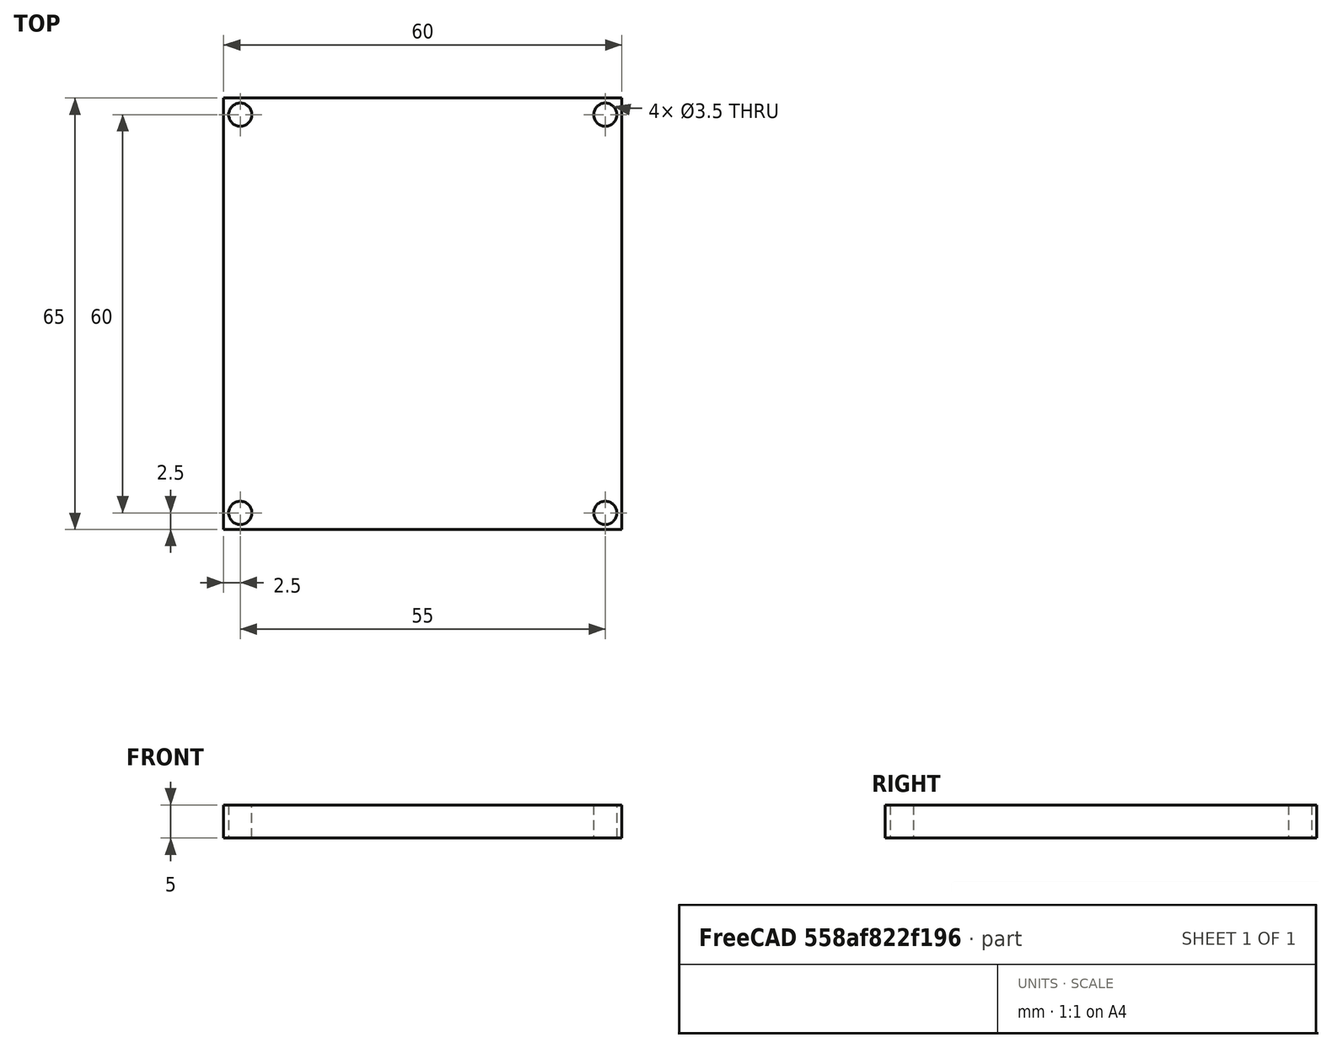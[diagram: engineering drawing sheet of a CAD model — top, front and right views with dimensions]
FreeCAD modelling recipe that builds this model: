
FCSTD DOCUMENT  (FreeCAD 0.19R)
Label: cover
License: All rights reserved
LicenseURL: http://en.wikipedia.org/wiki/All_rights_reserved
objects: PartDesign::CoordinateSystem×4, Sketcher::SketchObject×1, PartDesign::Pad×1, PartDesign::Body×1
note: 8 computed .brp shape members not serialized (recipe doc carries the construction recipe); baked Part::Feature solids carry a one-line shape summary decoded from their .brp

FEATURE [Sketcher::SketchObject] Sketch
  FullyConstrained = true
  MapMode = 5
  Support = -> [XY_Plane]
  sketch-geometry (8):
    g0: LineSegment StartX=-30 StartY=32.5 StartZ=0 EndX=30 EndY=32.5 EndZ=0
    g1: LineSegment StartX=30 StartY=32.5 StartZ=0 EndX=30 EndY=-32.5 EndZ=0
    g2: LineSegment StartX=30 StartY=-32.5 StartZ=0 EndX=-30 EndY=-32.5 EndZ=0
    g3: LineSegment StartX=-30 StartY=-32.5 StartZ=0 EndX=-30 EndY=32.5 EndZ=0
    g4: Circle CenterX=-27.5 CenterY=30 CenterZ=0 NormalX=0 NormalY=0 NormalZ=1 AngleXU=0 Radius=1.75
    g5: Circle CenterX=27.5 CenterY=30 CenterZ=0 NormalX=0 NormalY=0 NormalZ=1 AngleXU=0 Radius=1.75
    g6: Circle CenterX=-27.5 CenterY=-30 CenterZ=0 NormalX=0 NormalY=0 NormalZ=1 AngleXU=0 Radius=1.75
    g7: Circle CenterX=27.5 CenterY=-30 CenterZ=0 NormalX=0 NormalY=0 NormalZ=1 AngleXU=0 Radius=1.75
  constraints (22):
    c: Coincident(g0,g1)
    c: Coincident(g1,g2)
    c: Coincident(g2,g3)
    c: Coincident(g3,g0)
    c: Horizontal(g0)
    c: Vertical(g3)
    c: DistanceX(g0,g0) = 60
    c: DistanceY(g1,g1) = 65
    c: Symmetric(g2,g1,g-2)
    c: Symmetric(g1,g0,g-1)
    c: Equal(g6,g4)
    c: Equal(g4,g5)
    c: Equal(g5,g7)
    c: Diameter(g5) = 3.5
    c: DistanceY(g4,g0) = 2.5
    c: DistanceX(g0,g4) = 2.5
    c: DistanceY(g5,g0) = 2.5
    c: DistanceX(g5,g0) = 2.5
    c: DistanceX(g2,g6) = 2.5
    c: DistanceY(g2,g6) = 2.5
    c: DistanceX(g7,g1) = 2.5
    c: DistanceY(g1,g7) = 2.5
FEATURE [PartDesign::Pad] Pad
  Direction = (1,1,1)
  Length = 5
  Length2 = 100
  Profile = -> Sketch
  Type = 0
FEATURE [PartDesign::CoordinateSystem] LCS_1
  AttacherType = Attacher::AttachEngine3D
  MapMode = 11
  Placement = pos=(27.5,-30,0) rot=(0,0,1;1.5708rad)
  Support = -> [Pad]
FEATURE [PartDesign::CoordinateSystem] LCS_2
  AttacherType = Attacher::AttachEngine3D
  MapMode = 11
  Placement = pos=(-27.5,30,0) rot=(0,0,1;1.5708rad)
  Support = -> [Pad]
FEATURE [PartDesign::CoordinateSystem] LCS_3
  AttacherType = Attacher::AttachEngine3D
  MapMode = 11
  Placement = pos=(27.5,30,0) rot=(0,0,1;1.5708rad)
  Support = -> [Pad]
FEATURE [PartDesign::CoordinateSystem] LCS_4
  AttacherType = Attacher::AttachEngine3D
  MapMode = 11
  Placement = pos=(-27.5,-30,0) rot=(0,0,1;1.5708rad)
  Support = -> [Pad]
FEATURE [PartDesign::Body] Body
  Group = -> [Sketch,Pad,LCS_1,LCS_2,LCS_3,LCS_4]
  Origin = -> Origin
  Tip = -> Pad
